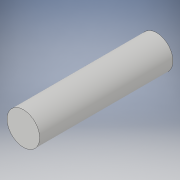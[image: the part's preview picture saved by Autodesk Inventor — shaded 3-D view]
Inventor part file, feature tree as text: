
AUTODESK INVENTOR PART (.ipt)
format: ipt  version: 2019 (Build 230136000, 136)  size: 89,088 bytes
history: native  units: mm
features: extrude x1, sketch x1
ambient origin geometry x8: Origin, YZ Plane, XZ Plane, XY Plane, X Axis, Y Axis, Z Axis, Center Point
bodies: Solid1 (feature_tree)
feature tree (2):
  extrude  "Extrusion1"  Depth=20.0mm TaperAngle=0.0deg
  sketch  "Sketch1"  dims[d0=4.9mm d1=20.0mm d2=0.0mm]
